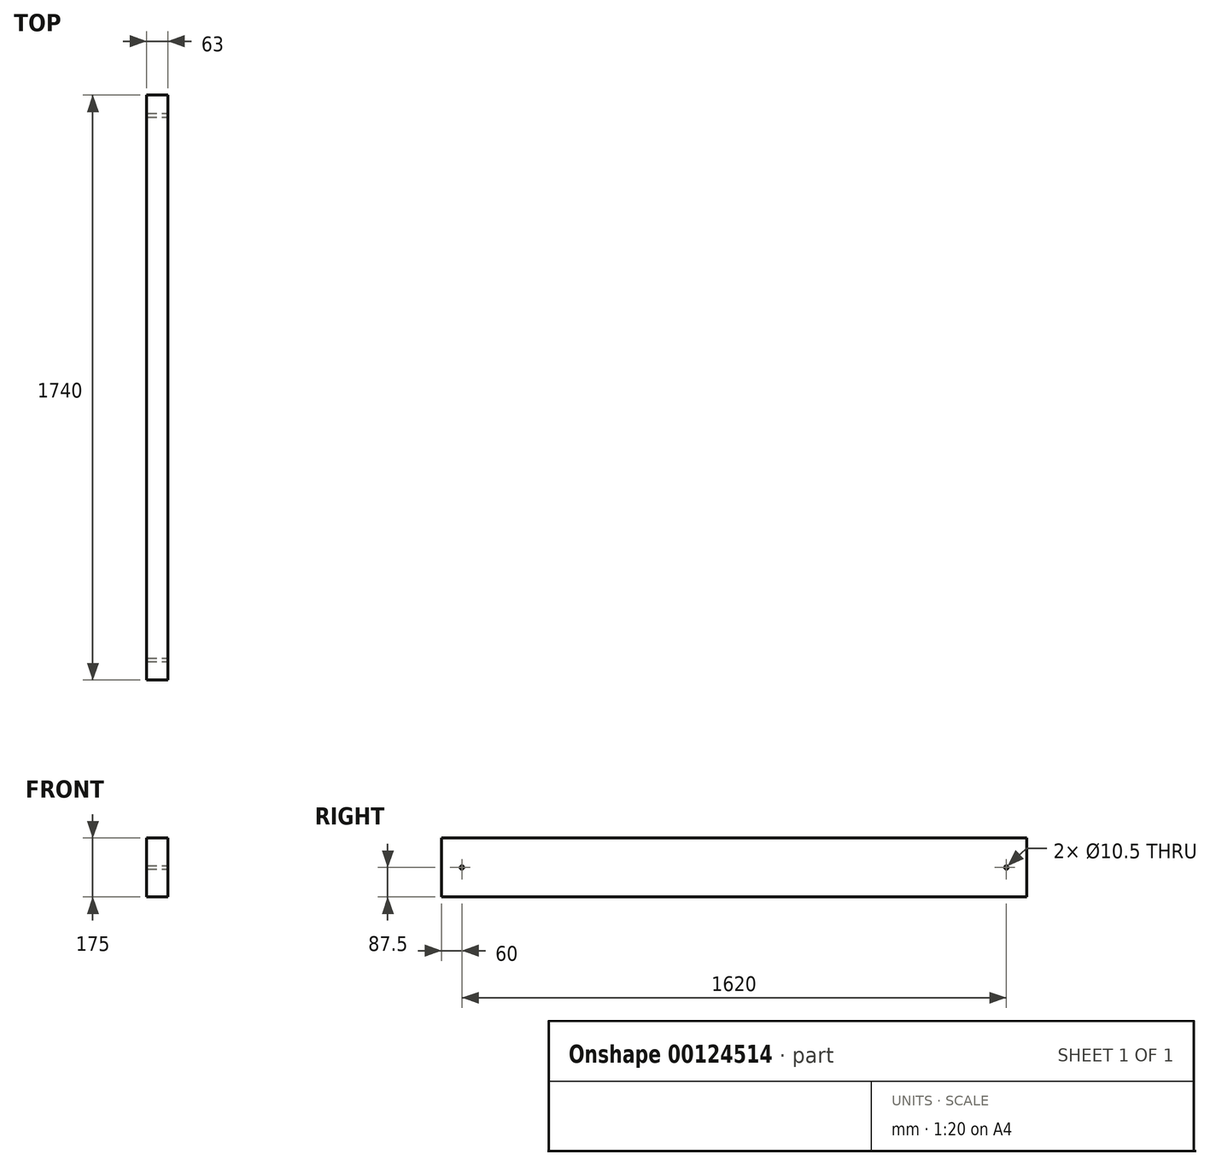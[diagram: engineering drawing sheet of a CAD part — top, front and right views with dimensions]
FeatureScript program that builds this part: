
annotation { "Feature Type Name" : "Feature", "Feature Type Description" : "" }
export const myFeature = defineFeature(function(context is Context, id is Id, definition is map)
    precondition{}
    {
        {
            var Q0;
            Q0=qCreatedBy(makeId("Front.planeOp"),FACE);
            var sketch = newSketch(context, id + "F0", { "sketchPlane" : qUnion([Q0])});
            skLineSegment(sketch, "E0.bottom", {"start": v(31.5, 87.5) * mm, "end": v(-31.5, 87.5) * mm});
            skLineSegment(sketch, "E0.top", {"start": v(31.5, -87.5) * mm, "end": v(-31.5, -87.5) * mm});
            skLineSegment(sketch, "E0.left", {"start": v(31.5, 87.5) * mm, "end": v(31.5, -87.5) * mm});
            skLineSegment(sketch, "E0.right", {"start": v(-31.5, 87.5) * mm, "end": v(-31.5, -87.5) * mm});
            skPoint(sketch, "E0.middle", {"position": v(0, 0) * mm});
            skSolve(sketch);
        }
        {
            var Q0;
            Q0=qSketchRegion(id+"F0",true);
            extrude(context, id + "F1", {"entities" : qUnion([Q0]), "endBound" : BoundingType.SYMMETRIC, "depth" : 1740 * mm});
        }
        {
            var Q0;
            Q0=makeQuery(id+"F1.opExtrude","SWEPT_FACE",FACE,{"disambiguationData":[OSD([sQuery(id+"F0.wireOp",EDGE,"E0.left")])]});
            var sketch = newSketch(context, id + "F2", { "sketchPlane" : qUnion([Q0])});
            skCircle(sketch, "E1", {"center": v(-810, 0) * mm, "radius": 5.25 * mm});
            skCircle(sketch, "E2", {"center": v(810, 0) * mm, "radius": 5.25 * mm});
            skSolve(sketch);
        }
        {
            var Q0;
            Q0=qSketchRegion(id+"F2",true);
            extrude(context, id + "F3", {"entities" : qUnion([Q0]), "operationType" : NewBodyOperationType.REMOVE, "endBound" : BoundingType.THROUGH_ALL, "oppositeDirection" : true, "depth" : 25 * mm});
        }
    });
